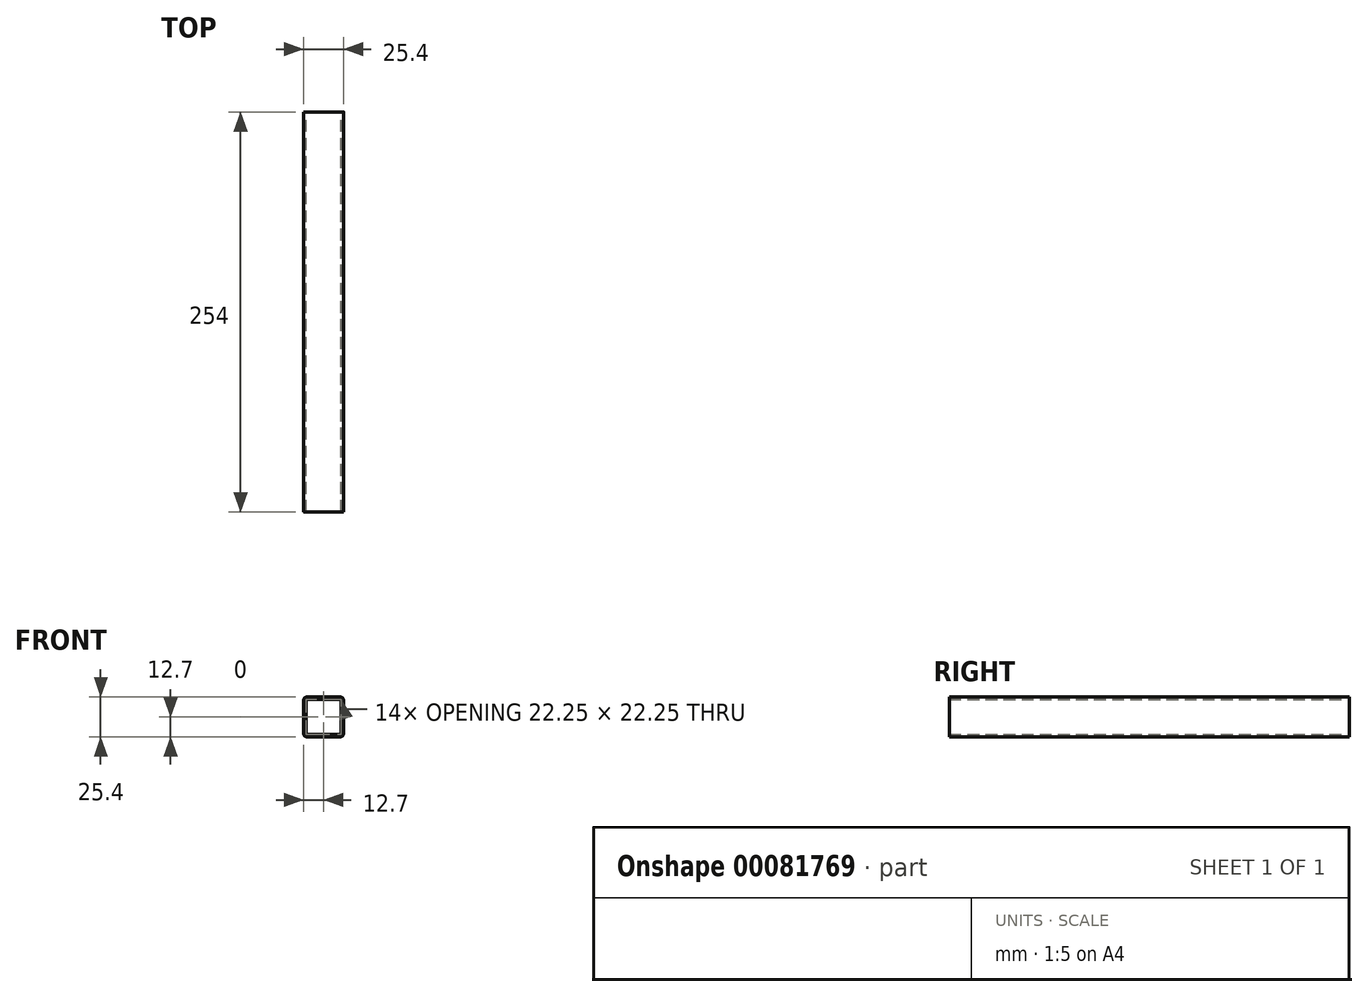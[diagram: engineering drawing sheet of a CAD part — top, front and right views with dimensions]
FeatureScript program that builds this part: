
annotation { "Feature Type Name" : "Feature", "Feature Type Description" : "" }
export const myFeature = defineFeature(function(context is Context, id is Id, definition is map)
    precondition{}
    {
        {
            var Q0;
            Q0=qCreatedBy(makeId("Front.planeOp"),FACE);
            var sketch = newSketch(context, id + "F0", { "sketchPlane" : qUnion([Q0])});
            skLineSegment(sketch, "E0.bottom", {"start": v(-10.62, -12.7) * mm, "end": v(10.62, -12.7) * mm});
            skLineSegment(sketch, "E0.top", {"start": v(-10.62, 12.7) * mm, "end": v(10.62, 12.7) * mm});
            skLineSegment(sketch, "E0.left", {"start": v(-12.7, -10.62) * mm, "end": v(-12.7, 10.62) * mm});
            skLineSegment(sketch, "E0.right", {"start": v(12.7, -10.62) * mm, "end": v(12.7, 10.62) * mm});
            skPoint(sketch, "E0.middle", {"position": v(0, 0) * mm});
            skLineSegment(sketch, "E1.bottom", {"start": v(10.62, -11.13) * mm, "end": v(-10.62, -11.13) * mm});
            skLineSegment(sketch, "E1.top", {"start": v(10.62, 11.13) * mm, "end": v(-10.62, 11.13) * mm});
            skLineSegment(sketch, "E1.left", {"start": v(11.13, -10.62) * mm, "end": v(11.13, 10.62) * mm});
            skLineSegment(sketch, "E1.right", {"start": v(-11.13, -10.62) * mm, "end": v(-11.13, 10.62) * mm});
            skPoint(sketch, "E2.visualSharp", {"position": v(-11.13, 11.13) * mm});
            skArc(sketch, "E2.filletArc", {"start": v(-10.62, 11.13) * mm, "mid": v(-10.98, 10.98) * mm, "end": v(-11.13, 10.62) * mm});
            skPoint(sketch, "E3.visualSharp", {"position": v(11.13, 11.13) * mm});
            skArc(sketch, "E3.filletArc", {"start": v(11.13, 10.62) * mm, "mid": v(10.98, 10.98) * mm, "end": v(10.62, 11.13) * mm});
            skPoint(sketch, "E4.visualSharp", {"position": v(11.13, -11.13) * mm});
            skArc(sketch, "E4.filletArc", {"start": v(10.62, -11.13) * mm, "mid": v(10.98, -10.98) * mm, "end": v(11.13, -10.62) * mm});
            skPoint(sketch, "E5.visualSharp", {"position": v(-11.13, -11.13) * mm});
            skArc(sketch, "E5.filletArc", {"start": v(-11.13, -10.62) * mm, "mid": v(-10.98, -10.98) * mm, "end": v(-10.62, -11.13) * mm});
            skPoint(sketch, "E6.visualSharp", {"position": v(-12.7, 12.7) * mm});
            skArc(sketch, "E6.filletArc", {"start": v(-10.62, 12.7) * mm, "mid": v(-12.09, 12.09) * mm, "end": v(-12.7, 10.62) * mm});
            skPoint(sketch, "E7.visualSharp", {"position": v(12.7, 12.7) * mm});
            skArc(sketch, "E7.filletArc", {"start": v(12.7, 10.62) * mm, "mid": v(12.09, 12.09) * mm, "end": v(10.62, 12.7) * mm});
            skPoint(sketch, "E8.visualSharp", {"position": v(-12.7, -12.7) * mm});
            skArc(sketch, "E8.filletArc", {"start": v(-12.7, -10.62) * mm, "mid": v(-12.09, -12.09) * mm, "end": v(-10.62, -12.7) * mm});
            skPoint(sketch, "E9.visualSharp", {"position": v(12.7, -12.7) * mm});
            skArc(sketch, "E9.filletArc", {"start": v(10.62, -12.7) * mm, "mid": v(12.09, -12.09) * mm, "end": v(12.7, -10.62) * mm});
            skSolve(sketch);
        }
        {
            var Q0;
            Q0=qSketchRegion(id+"F0",true);
            extrude(context, id + "F1", {"entities" : qUnion([Q0]), "depth" : 254 * mm});
        }
    });
